# Revit family: Витрина уличная «Буккроссинг» красная Арт 13172
name_source: partatom
category: Антураж
revit_build: Autodesk Revit 2018 (Build: 20180423_1000(x64)
units: mm (PartAtom-declared; Revit-internal decimal feet)

## family parameters
Всегда вертикально = Да
Источник визуального образа = Геометрия семейства
На основе рабочей плоскости = Нет
Общий = Нет
При загрузке вырезать с полостями = Нет
Точка расчета площади = Нет

## types (1)
- Витрина уличная Буккроссинг компактная
    URL = https://hobbyka.ru
    Артикул товара = Арт. 13172
    Высота = 2200 мм
    Группа модели = Павильоны, остановки, курилки, буккроссинг
    Длина = 1100 мм
    Изготовитель = ООО «Хоббика»
    Изображение типоразмера = Витрина уличная «Буккроссинг» красная 13172.jpg
    Количество секций = 4
    Материал изделия = Сталь
    Описание = Витрина уличная «Буккроссинг» красная
    Ширина = 600 мм

## geometry (parser evidence)
native form markers: Sweep x1
no freeform markers — native parametric forms only
